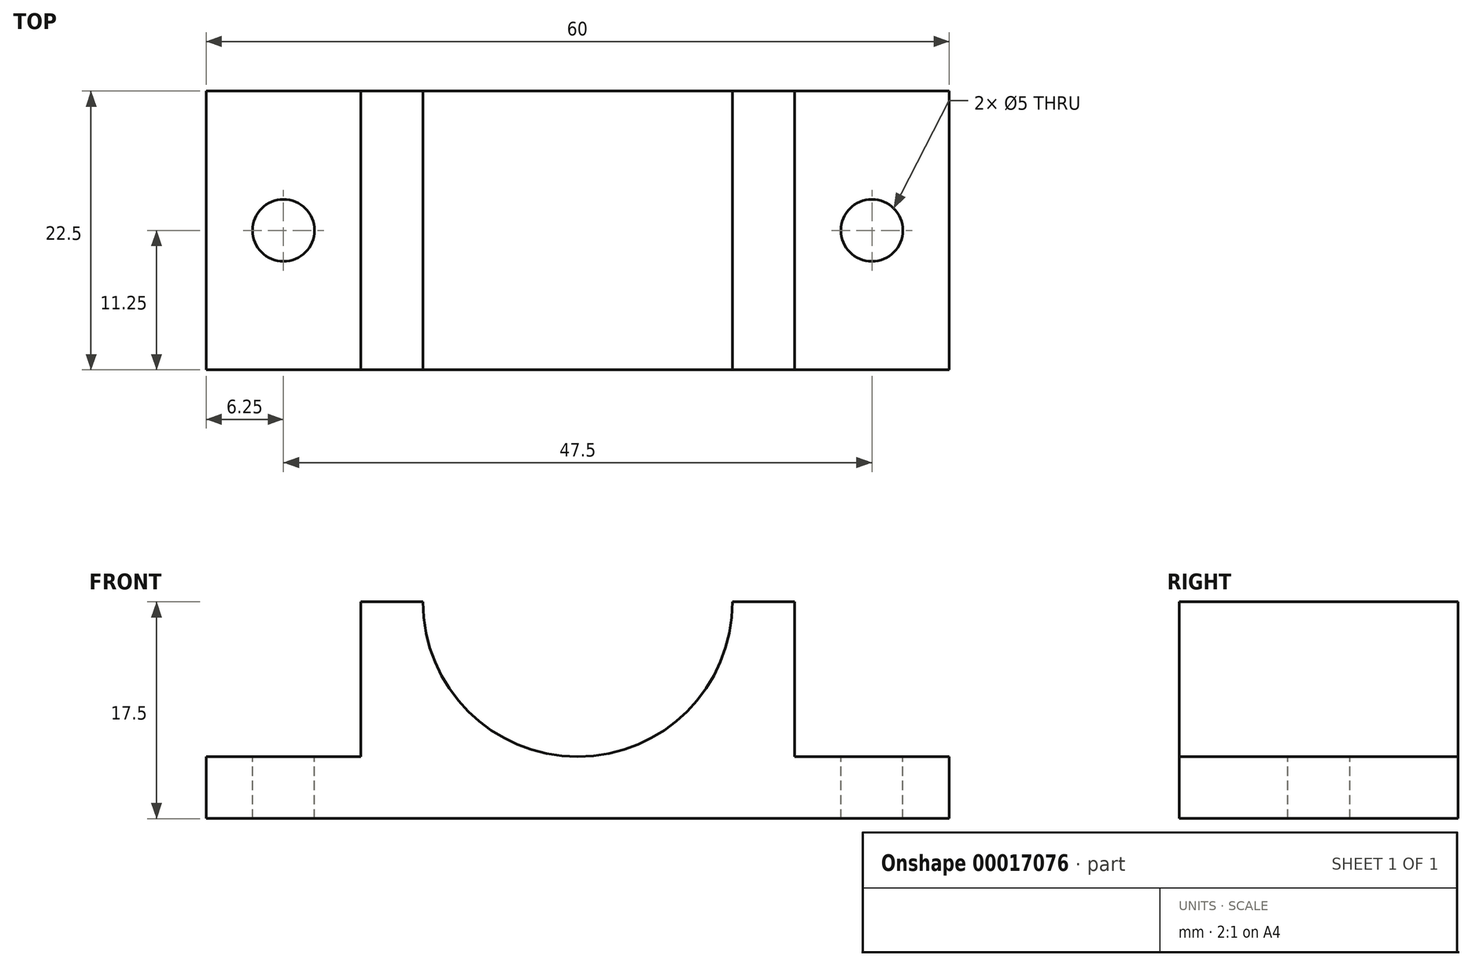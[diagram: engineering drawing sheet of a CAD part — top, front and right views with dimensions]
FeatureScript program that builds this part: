
annotation { "Feature Type Name" : "Feature", "Feature Type Description" : "" }
export const myFeature = defineFeature(function(context is Context, id is Id, definition is map)
    precondition{}
    {
        {
            var Q0;
            Q0=qCreatedBy(makeId("Front.planeOp"),FACE);
            var sketch = newSketch(context, id + "F0", { "sketchPlane" : qUnion([Q0])});
            skLineSegment(sketch, "E0", {"start": v(-37.3, -13.55) * mm, "end": v(-37.3, -18.55) * mm});
            skLineSegment(sketch, "E1", {"start": v(-37.3, -18.55) * mm, "end": v(22.7, -18.55) * mm});
            skLineSegment(sketch, "E2", {"start": v(22.7, -18.55) * mm, "end": v(22.7, -13.55) * mm});
            skLineSegment(sketch, "E3", {"start": v(22.7, -13.55) * mm, "end": v(10.2, -13.55) * mm});
            skLineSegment(sketch, "E4", {"start": v(10.2, -13.55) * mm, "end": v(10.2, -1.05) * mm});
            skLineSegment(sketch, "E5", {"start": v(10.2, -1.05) * mm, "end": v(-24.8, -1.05) * mm});
            skLineSegment(sketch, "E6", {"start": v(-24.8, -1.05) * mm, "end": v(-24.8, -13.55) * mm});
            skLineSegment(sketch, "E7", {"start": v(-24.8, -13.55) * mm, "end": v(-37.3, -13.55) * mm});
            skCircle(sketch, "E8", {"center": v(-7.3, -1.05) * mm, "radius": 12.5 * mm});
            skSolve(sketch);
        }
        {
            var Q0;
            Q0=makeQuery(id+"F0.imprint","IMPRINT",FACE,{"disambiguationData":[TD([[makeQuery(id+"F0.imprint","IMPRINT",EDGE,{"derivedFrom":sQuery(id+"F0.wireOp",EDGE,"E0")}),1.0]])]});
            extrude(context, id + "F1", {"entities" : qUnion([Q0]), "depth" : 22.5 * mm});
        }
        {
            var Q0;
            Q0=makeQuery(id+"F1.opExtrude","SWEPT_FACE",FACE,{"disambiguationData":[OSD([sQuery(id+"F0.wireOp",EDGE,"E3")])]});
            var sketch = newSketch(context, id + "F2", { "sketchPlane" : qUnion([Q0])});
            skCircle(sketch, "E9", {"center": v(16.45, -11.25) * mm, "radius": 2.5 * mm});
            skSolve(sketch);
        }
        {
            var Q0;
            Q0=makeQuery(id+"F2.imprint","IMPRINT",FACE,{"disambiguationData":[TD([[makeQuery(id+"F2.imprint","IMPRINT",EDGE,{"derivedFrom":sQuery(id+"F2.wireOp",EDGE,"E9")}),1.0]])]});
            extrude(context, id + "F3", {"entities" : qUnion([Q0]), "operationType" : NewBodyOperationType.REMOVE, "endBound" : BoundingType.THROUGH_ALL, "oppositeDirection" : true, "depth" : 25 * mm});
        }
        {
            var Q0;
            Q0=makeQuery(id+"F1.opExtrude","SWEPT_FACE",FACE,{"disambiguationData":[OSD([sQuery(id+"F0.wireOp",EDGE,"E7")])]});
            var sketch = newSketch(context, id + "F4", { "sketchPlane" : qUnion([Q0])});
            skCircle(sketch, "E10", {"center": v(-31.05, -11.25) * mm, "radius": 2.5 * mm});
            skSolve(sketch);
        }
        {
            var Q0;
            Q0=makeQuery(id+"F4.imprint","IMPRINT",FACE,{"disambiguationData":[TD([[makeQuery(id+"F4.imprint","IMPRINT",EDGE,{"derivedFrom":sQuery(id+"F4.wireOp",EDGE,"E10")}),1.0]])]});
            extrude(context, id + "F5", {"entities" : qUnion([Q0]), "operationType" : NewBodyOperationType.REMOVE, "endBound" : BoundingType.THROUGH_ALL, "oppositeDirection" : true, "depth" : 25 * mm});
        }
    });
